annotation { "Feature Type Name" : "Feature", "Feature Type Description" : "" }
export const myFeature = defineFeature(function(context is Context, id is Id, definition is map)
    precondition{}
    {
        {
            var Q0;
            Q0=qCreatedBy(makeId("Front.planeOp"),FACE);
            var sketch = newSketch(context, id + "F0", { "sketchPlane" : qUnion([Q0])});
            skLineSegment(sketch, "E0", {"start": v(0, 0) * mm, "end": v(-9144, 0) * mm});
            skLineSegment(sketch, "E1", {"start": v(-4572, 0) * mm, "end": v(-4572, 2286) * mm});
            skLineSegment(sketch, "E2", {"start": v(-4572, 2286) * mm, "end": v(0, 0) * mm});
            skLineSegment(sketch, "E3", {"start": v(-4572, 2286) * mm, "end": v(-9144, 0) * mm});
            skLineSegment(sketch, "E4", {"start": v(0, 0) * mm, "end": v(0, -6096) * mm});
            skLineSegment(sketch, "E5", {"start": v(-9144, 0) * mm, "end": v(-9144, -6096) * mm});
            skLineSegment(sketch, "E6", {"start": v(-9144, -6096) * mm, "end": v(0, -6096) * mm});
            skLineSegment(sketch, "E7", {"start": v(-4572, -6096) * mm, "end": v(-4572, -3962.4) * mm});
            skLineSegment(sketch, "E8", {"start": v(-4572, -3962.4) * mm, "end": v(-3657.6, -3962.4) * mm});
            skLineSegment(sketch, "E9", {"start": v(-3657.6, -3962.4) * mm, "end": v(-3657.6, -6096) * mm});
            skLineSegment(sketch, "E10", {"start": v(-3785.22, -1609.66) * mm, "end": v(-1042.02, -1609.66) * mm});
            skLineSegment(sketch, "E11", {"start": v(-1042.02, -1609.66) * mm, "end": v(-1042.02, -2524.06) * mm});
            skLineSegment(sketch, "E12", {"start": v(-1042.02, -2524.06) * mm, "end": v(-3785.22, -2524.06) * mm});
            skLineSegment(sketch, "E13", {"start": v(-3785.22, -1609.66) * mm, "end": v(-3785.22, -2524.06) * mm});
            skLineSegment(sketch, "E14", {"start": v(-2413.62, -1609.66) * mm, "end": v(-2413.62, -2524.06) * mm});
            skLineSegment(sketch, "E15", {"start": v(-3785.22, -2066.86) * mm, "end": v(-1042.02, -2066.86) * mm});
            skLineSegment(sketch, "E16", {"start": v(-8581.5, -1736.3) * mm, "end": v(-7057.5, -1736.3) * mm});
            skLineSegment(sketch, "E17", {"start": v(-7057.5, -1736.3) * mm, "end": v(-7057.5, -2650.7) * mm});
            skLineSegment(sketch, "E18", {"start": v(-7057.5, -2650.7) * mm, "end": v(-8581.5, -2650.7) * mm});
            skLineSegment(sketch, "E19", {"start": v(-8581.5, -1736.3) * mm, "end": v(-8581.5, -2650.7) * mm});
            skLineSegment(sketch, "E20", {"start": v(-7819.5, -1736.3) * mm, "end": v(-7819.5, -2650.7) * mm});
            skLineSegment(sketch, "E21", {"start": v(-8581.5, -2193.5) * mm, "end": v(-7057.5, -2193.5) * mm});
            skLineSegment(sketch, "E22", {"start": v(-9144, -6096) * mm, "end": v(-9144, -6705.6) * mm});
            skLineSegment(sketch, "E23", {"start": v(-9144, -6705.6) * mm, "end": v(0, -6705.6) * mm});
            skLineSegment(sketch, "E24", {"start": v(0, -6705.6) * mm, "end": v(0, -6096) * mm});
            skSolve(sketch);
        }
        {
            var Q0;
            Q0 = qSketchRegion(id + "F0", true);
            extrude(context, id + "F1", {"entities" : qUnion([Q0]), "depth" : 12192 * mm, "offsetDistance" : 30.48 * mm});
        }
        {
            var Q0;
            {var subQ4=sQuery(id+"F0.wireOp",EDGE,"E22");Q0=makeQuery(id+"F0.imprint","IMPRINT",FACE,{"disambiguationData":[TD([[makeQuery(id+"F0.imprint","IMPRINT",EDGE,{"derivedFrom":subQ4}),1.0]])]});}
            extrude(context, id + "F2", {"entities" : qUnion([Q0]), "operationType" : NewBodyOperationType.ADD, "endBound" : BoundingType.SYMMETRIC, "oppositeDirection" : true, "depth" : 2865.12 * mm, "offsetDistance" : 30.48 * mm});
        }
        {
            var Q0;
            {var subQ0=sQuery(id+"F0.wireOp",EDGE,"E6");Q0=makeQuery(id+"F2.boolean.opBoolean","MERGE",FACE,{"derivedFrom":[makeQuery(id+"F1.opExtrude","SWEPT_FACE",FACE,{"disambiguationData":[OSD([subQ0])]}),makeQuery(id+"F2.opExtrude","SWEPT_FACE",FACE,{"disambiguationData":[OSD([subQ0])]})]});}
            var sketch = newSketch(context, id + "F3", { "sketchPlane" : qUnion([Q0])});
            skText(sketch, "E25", { "text": "CARTERS HOUSE", "fontName": "OpenSans-Bold.ttf"});
            const initialGuessF3  = {"E25": [-7.24829, 0.52513, 1, 0, 0.56282]};
            skSetInitialGuess(sketch, initialGuessF3);
            skSolve(sketch);
        }
        {
            var Q0;
            Q0 = qSketchRegion(id + "F3", true);
            extrude(context, id + "F4", {"entities" : qUnion([Q0]), "operationType" : NewBodyOperationType.ADD, "endBound" : BoundingType.SYMMETRIC, "depth" : 1036.32 * mm, "offsetDistance" : 30.48 * mm});
        }
    });